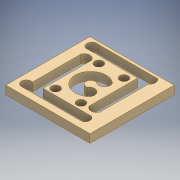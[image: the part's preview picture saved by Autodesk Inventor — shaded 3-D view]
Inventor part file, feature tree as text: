
AUTODESK INVENTOR PART (.ipt)
format: ipt  version: 2016 (Build 200138000, 138)  size: 389,120 bytes
history: native  units: mm
features: sketch x3, extrude x1, hole x1, emboss x1, projected_geometry x1
ambient origin geometry x8: Origin, YZ Plane, XZ Plane, XY Plane, X Axis, Y Axis, Z Axis, Center Point
bodies: Solid1 (feature_tree)
feature tree (7):
  extrude  "Extrusion1"  Depth=127.0mm
  hole  "Hole1"  [1 undecoded]
  emboss  "Emboss1"
  sketch  "Sketch1"  dims[d0=127.0mm d1=127.0mm]
  sketch  "Sketch2"  dims[d2=12.7mm d3=0.0mm d4=12.7mm]
  sketch  "Sketch3"  dims[d5=12.7mm d6=12.7mm d7=12.7mm d8=12.7mm d9=6.0mm d10=4.0mm d11=2.0mm d12=90.0deg d13=8.0mm d14=20.594885mm d15=12.7mm d16=0.0mm]
  projected_geometry  "Projected Loop1"
note: 1 required parameter value undecoded (feature->parameter linkage not recoverable at this tier; creation-order binding heuristic only, values carry confidence <= 0.55)
